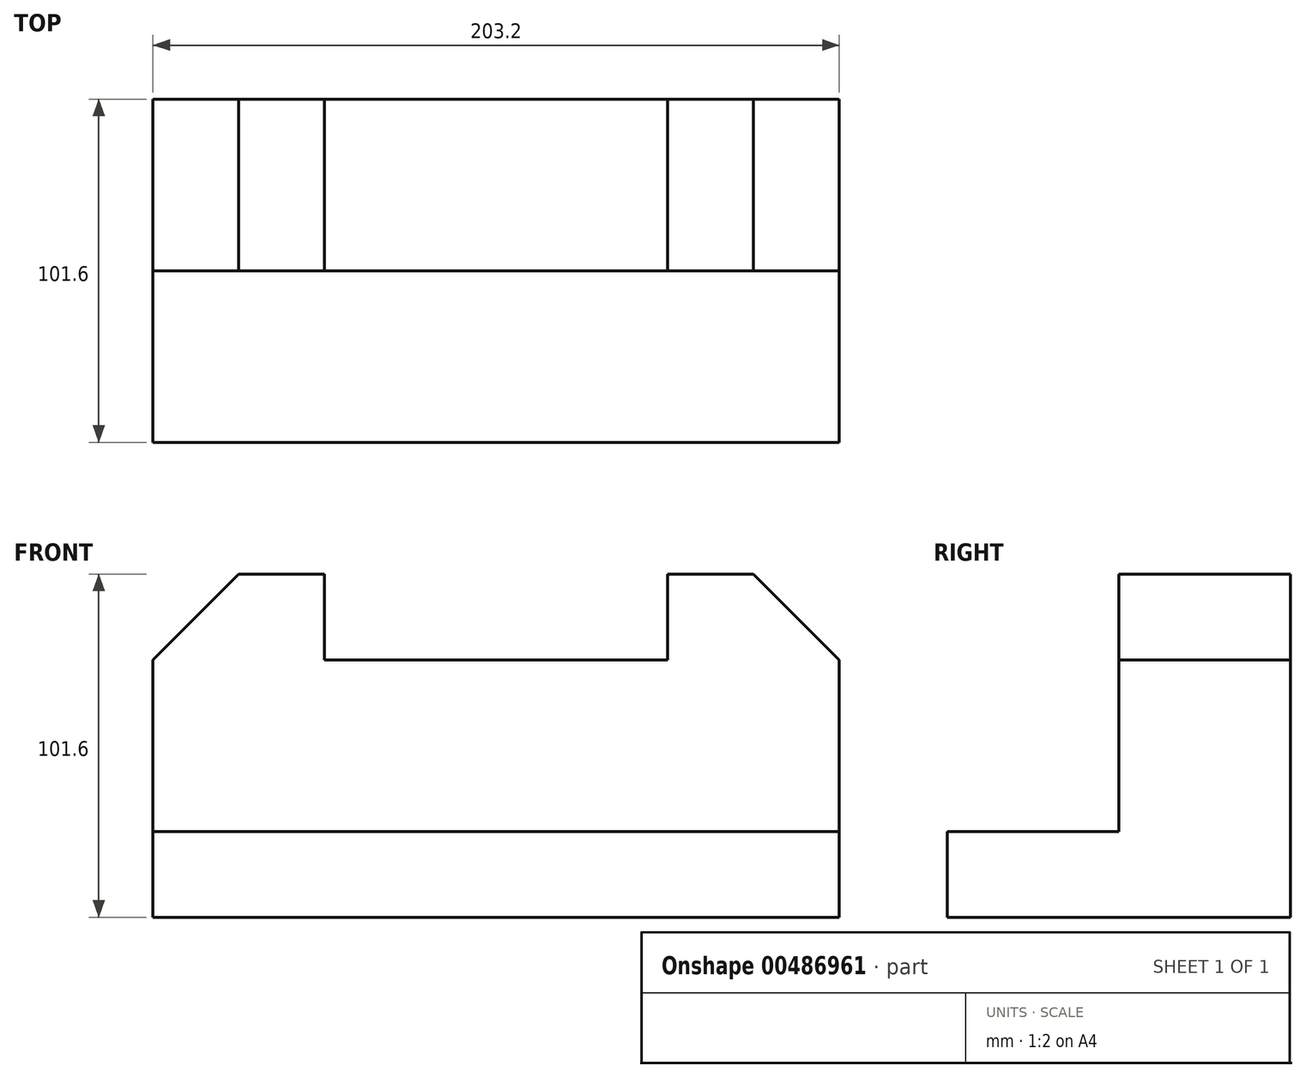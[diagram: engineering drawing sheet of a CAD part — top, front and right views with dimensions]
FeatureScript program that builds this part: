
annotation { "Feature Type Name" : "Feature", "Feature Type Description" : "" }
export const myFeature = defineFeature(function(context is Context, id is Id, definition is map)
    precondition{}
    {
        {
            var Q0;
            Q0=qCreatedBy(makeId("Right.planeOp"),FACE);
            var sketch = newSketch(context, id + "F0", { "sketchPlane" : qUnion([Q0])});
            skLineSegment(sketch, "E0.bottom", {"start": v(-37.92, -0.54) * mm, "end": v(12.88, -0.54) * mm});
            skLineSegment(sketch, "E0.top", {"start": v(-37.92, -25.94) * mm, "end": v(63.68, -25.94) * mm});
            skLineSegment(sketch, "E0.left", {"start": v(-37.92, -0.54) * mm, "end": v(-37.92, -25.94) * mm});
            skLineSegment(sketch, "E0.right", {"start": v(63.68, -0.54) * mm, "end": v(63.68, -25.94) * mm});
            skLineSegment(sketch, "E1.top", {"start": v(63.68, 75.66) * mm, "end": v(12.88, 75.66) * mm});
            skLineSegment(sketch, "E1.left", {"start": v(63.68, -0.54) * mm, "end": v(63.68, 75.66) * mm});
            skLineSegment(sketch, "E1.right", {"start": v(12.88, -0.54) * mm, "end": v(12.88, 75.66) * mm});
            skSolve(sketch);
        }
        {
            var Q0;
            Q0 = qSketchRegion(id + "F0", true);
            extrude(context, id + "F1", {"entities" : qUnion([Q0]), "depth" : 203.2 * mm});
        }
        {
            var Q0;
            Q0=makeQuery(id+"F1.opExtrude","SWEPT_FACE",FACE,{"disambiguationData":[OSD([sQuery(id+"F0.wireOp",EDGE,"E0.bottom")])]});
            var sketch = newSketch(context, id + "F2", { "sketchPlane" : qUnion([Q0])});
            skLineSegment(sketch, "E2.bottom", {"start": v(-37.92, -50.8) * mm, "end": v(-12.52, -50.8) * mm});
            skLineSegment(sketch, "E2.top", {"start": v(-37.92, -152.4) * mm, "end": v(-12.52, -152.4) * mm});
            skLineSegment(sketch, "E2.left", {"start": v(-37.92, -50.8) * mm, "end": v(-37.92, -152.4) * mm});
            skLineSegment(sketch, "E2.right", {"start": v(-12.52, -50.8) * mm, "end": v(-12.52, -152.4) * mm});
            skSolve(sketch);
        }
        {
            var Q0;
            Q0 = qSketchRegion(id + "F2", true);
            var Q1;
            Q1=makeQuery(id+"F2.imprint","IMPRINT",FACE,{"disambiguationData":[TD([[makeQuery(id+"F2.imprint","IMPRINT",EDGE,{"derivedFrom":sQuery(id+"F2.wireOp",EDGE,"E2.bottom")}),-1.0]])]});
            extrude(context, id + "F3", {"entities" : qUnion([Q0, Q1]), "operationType" : NewBodyOperationType.REMOVE, "oppositeDirection" : true, "depth" : 25.4 * mm});
        }
        {
            var Q0;
            Q0=makeQuery(id+"F1.opExtrude","SWEPT_FACE",FACE,{"disambiguationData":[OSD([sQuery(id+"F0.wireOp",EDGE,"E1.top")])]});
            var sketch = newSketch(context, id + "F4", { "sketchPlane" : qUnion([Q0])});
            skLineSegment(sketch, "E3.bottom", {"start": v(63.68, -50.8) * mm, "end": v(12.88, -50.8) * mm});
            skLineSegment(sketch, "E3.top", {"start": v(63.68, -152.4) * mm, "end": v(12.88, -152.4) * mm});
            skLineSegment(sketch, "E3.left", {"start": v(63.68, -50.8) * mm, "end": v(63.68, -152.4) * mm});
            skLineSegment(sketch, "E3.right", {"start": v(12.88, -50.8) * mm, "end": v(12.88, -152.4) * mm});
            skSolve(sketch);
        }
        {
            var Q0;
            Q0 = qSketchRegion(id + "F4", true);
            var Q1;
            Q1=makeQuery(id+"F4.imprint","IMPRINT",FACE,{"disambiguationData":[TD([[makeQuery(id+"F4.imprint","IMPRINT",EDGE,{"derivedFrom":sQuery(id+"F4.wireOp",EDGE,"E3.bottom")}),1.0]])]});
            extrude(context, id + "F5", {"entities" : qUnion([Q0, Q1]), "operationType" : NewBodyOperationType.REMOVE, "oppositeDirection" : true, "depth" : 25.4 * mm});
        }
        {
            var Q0;
            Q0=makeQuery(id+"F1.opExtrude","SWEPT_FACE",FACE,{"disambiguationData":[OSD([sQuery(id+"F0.wireOp",EDGE,"E1.right")])]});
            var sketch = newSketch(context, id + "F6", { "sketchPlane" : qUnion([Q0])});
            skLineSegment(sketch, "E4", {"start": v(177.8, 75.66) * mm, "end": v(203.2, 50.26) * mm});
            skLineSegment(sketch, "E5", {"start": v(25.4, 75.66) * mm, "end": v(0, 50.26) * mm});
            skSolve(sketch);
        }
        {
            var Q0;
            Q0 = qSketchRegion(id + "F6", true);
            var Q1;
            {var subQ0=sQuery(id+"F6.wireOp",EDGE,"E4");Q1=makeQuery(id+"F6.imprint","IMPRINT",FACE,{"disambiguationData":[TD([[makeQuery(id+"F6.imprint","IMPRINT",EDGE,{"derivedFrom":subQ0}),1.0]])]});}
            var Q2;
            {var subQ0=sQuery(id+"F6.wireOp",EDGE,"E5");Q2=makeQuery(id+"F6.imprint","IMPRINT",FACE,{"disambiguationData":[TD([[makeQuery(id+"F6.imprint","IMPRINT",EDGE,{"derivedFrom":subQ0}),-1.0]])]});}
            extrude(context, id + "F7", {"entities" : qUnion([Q0, Q1, Q2]), "operationType" : NewBodyOperationType.REMOVE, "oppositeDirection" : true, "depth" : 50.8 * mm});
        }
        {
            var Q0;
            Q0=makeQuery(id+"F1.opExtrude","SWEPT_FACE",FACE,{"disambiguationData":[OSD([sQuery(id+"F0.wireOp",EDGE,"E1.top")])]});
            var sketch = newSketch(context, id + "F8", { "sketchPlane" : qUnion([Q0])});
            skLineSegment(sketch, "E6.bottom", {"start": v(50.8, 63.68) * mm, "end": v(152.4, 63.68) * mm});
            skLineSegment(sketch, "E6.top", {"start": v(50.8, 12.88) * mm, "end": v(152.4, 12.88) * mm});
            skLineSegment(sketch, "E6.left", {"start": v(50.8, 63.68) * mm, "end": v(50.8, 12.88) * mm});
            skLineSegment(sketch, "E6.right", {"start": v(152.4, 63.68) * mm, "end": v(152.4, 12.88) * mm});
            skSolve(sketch);
        }
        {
            var Q0;
            Q0=makeQuery(id+"F8.imprint","IMPRINT",FACE,{"disambiguationData":[TD([[makeQuery(id+"F8.imprint","IMPRINT",EDGE,{"derivedFrom":sQuery(id+"F8.wireOp",EDGE,"E6.bottom")}),1.0]])]});
            extrude(context, id + "F9", {"entities" : qUnion([Q0]), "operationType" : NewBodyOperationType.REMOVE, "oppositeDirection" : true, "depth" : 25.4 * mm});
        }
    });
